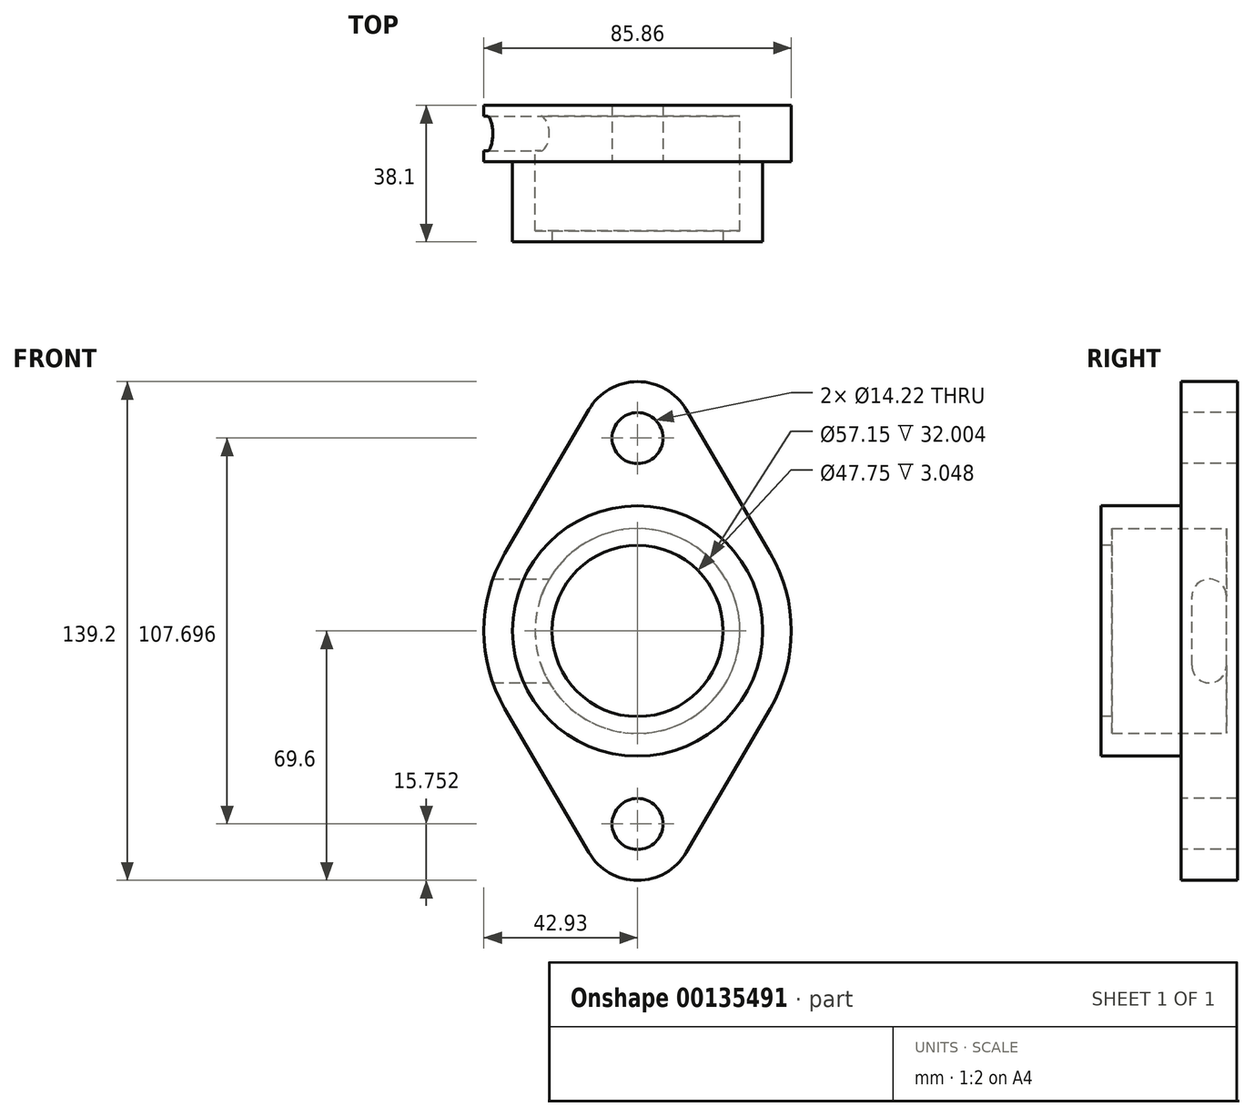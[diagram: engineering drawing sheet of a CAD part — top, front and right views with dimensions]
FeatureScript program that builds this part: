
annotation { "Feature Type Name" : "Feature", "Feature Type Description" : "" }
export const myFeature = defineFeature(function(context is Context, id is Id, definition is map)
    precondition{}
    {
        {
            var Q0;
            Q0=qCreatedBy(makeId("Front.planeOp"),FACE);
            var sketch = newSketch(context, id + "F0", { "sketchPlane" : qUnion([Q0])});
            skCircle(sketch, "E0", {"center": v(0, 0) * mm, "radius": 34.93 * mm});
            skCircle(sketch, "E1", {"center": v(0, 53.85) * mm, "radius": 7.11 * mm});
            skCircle(sketch, "E2", {"center": v(0, -53.85) * mm, "radius": 7.11 * mm});
            skLineSegment(sketch, "E3", {"start": v(-37.06, 21.67) * mm, "end": v(-13.6, 61.8) * mm});
            skLineSegment(sketch, "E4", {"start": v(37.06, 21.67) * mm, "end": v(13.6, 61.8) * mm});
            skLineSegment(sketch, "E5", {"start": v(-37.06, -21.67) * mm, "end": v(-13.6, -61.8) * mm});
            skLineSegment(sketch, "E6", {"start": v(37.06, -21.67) * mm, "end": v(13.6, -61.8) * mm});
            skArc(sketch, "E7", {"start": v(-37.06, 21.67) * mm, "mid": v(-42.93, 0) * mm, "end": v(-37.06, -21.67) * mm});
            skArc(sketch, "E8", {"start": v(-13.6, -61.8) * mm, "mid": v(0, -69.6) * mm, "end": v(13.6, -61.8) * mm});
            skArc(sketch, "E9", {"start": v(37.06, -21.67) * mm, "mid": v(42.93, 0) * mm, "end": v(37.06, 21.67) * mm});
            skArc(sketch, "E10", {"start": v(-13.6, 61.8) * mm, "mid": v(0, 69.6) * mm, "end": v(13.6, 61.8) * mm});
            skSolve(sketch);
        }
        {
            var Q0;
            Q0=makeQuery(id+"F0.imprint","IMPRINT",FACE,{"disambiguationData":[TD([[makeQuery(id+"F0.imprint","IMPRINT",EDGE,{"derivedFrom":sQuery(id+"F0.wireOp",EDGE,"E0")}),1.0]])]});
            extrude(context, id + "F1", {"entities" : qUnion([Q0]), "endBound" : BoundingType.SYMMETRIC, "depth" : 31.5 * mm});
        }
        {
            var Q0;
            Q0=makeQuery(id+"F0.imprint","IMPRINT",FACE,{"disambiguationData":[TD([[makeQuery(id+"F0.imprint","IMPRINT",EDGE,{"derivedFrom":sQuery(id+"F0.wireOp",EDGE,"E0")}),-1.0]])]});
            extrude(context, id + "F2", {"entities" : qUnion([Q0]), "operationType" : NewBodyOperationType.ADD, "oppositeDirection" : true, "depth" : 15.75 * mm});
        }
        {
            var Q0;
            Q0=makeQuery(id+"F0.imprint","IMPRINT",FACE,{"disambiguationData":[TD([[makeQuery(id+"F0.imprint","IMPRINT",EDGE,{"derivedFrom":sQuery(id+"F0.wireOp",EDGE,"E0")}),1.0]])]});
            extrude(context, id + "F3", {"entities" : qUnion([Q0]), "operationType" : NewBodyOperationType.ADD, "depth" : 22.35 * mm});
        }
        {
            var Q0;
            Q0=qCreatedBy(makeId("Front.planeOp"),FACE);
            var sketch = newSketch(context, id + "F4", { "sketchPlane" : qUnion([Q0])});
            skCircle(sketch, "E11", {"center": v(0, 0) * mm, "radius": 28.58 * mm});
            skSolve(sketch);
        }
        {
            var Q0;
            Q0 = qSketchRegion(id + "F4", true);
            extrude(context, id + "F5", {"entities" : qUnion([Q0]), "operationType" : NewBodyOperationType.REMOVE, "depth" : 19.3 * mm});
        }
        {
            var Q0;
            Q0=makeQuery(id+"F3.opExtrude","CAP_FACE",FACE,{"disambiguationData":[OSD([sQuery(id+"F0.wireOp",EDGE,"E0")])],"isStart":false});
            cPlane(context, id + "F6", {"entities" : qUnion([Q0]), "cplaneType" : CPlaneType.OFFSET, "offset" : 0 * mm, "width" : 152.4 * mm, "height" : 152.4 * mm});
        }
        {
            var Q0;
            Q0=qCreatedBy(id+"F6.planeOp",FACE);
            var sketch = newSketch(context, id + "F7", { "sketchPlane" : qUnion([Q0])});
            skCircle(sketch, "E12", {"center": v(0, 0) * mm, "radius": 23.88 * mm});
            skSolve(sketch);
        }
        {
            var Q0;
            Q0 = qSketchRegion(id + "F7", true);
            extrude(context, id + "F8", {"entities" : qUnion([Q0]), "operationType" : NewBodyOperationType.REMOVE, "oppositeDirection" : true, "depth" : 3.05 * mm});
        }
        {
            var Q0;
            Q0=qCreatedBy(makeId("Right.planeOp"),FACE);
            var sketch = newSketch(context, id + "F9", { "sketchPlane" : qUnion([Q0])});
            skLineSegment(sketch, "E13", {"start": v(12.7, -9.65) * mm, "end": v(12.7, 9.65) * mm});
            skLineSegment(sketch, "E14", {"start": v(3.05, -9.65) * mm, "end": v(3.05, 9.65) * mm});
            skArc(sketch, "E15", {"start": v(12.7, 9.65) * mm, "mid": v(7.87, 14.48) * mm, "end": v(3.05, 9.65) * mm});
            skArc(sketch, "E16", {"start": v(12.7, -9.65) * mm, "mid": v(7.87, -14.48) * mm, "end": v(3.05, -9.65) * mm});
            skSolve(sketch);
        }
        {
            var Q0;
            Q0 = qSketchRegion(id + "F9", true);
            extrude(context, id + "F10", {"entities" : qUnion([Q0]), "operationType" : NewBodyOperationType.REMOVE, "endBound" : BoundingType.UP_TO_NEXT, "oppositeDirection" : true, "depth" : 25.4 * mm});
        }
        {
            var Q0;
            Q0=makeQuery(id+"F4.imprint","IMPRINT",FACE,{"disambiguationData":[TD([[makeQuery(id+"F4.imprint","IMPRINT",EDGE,{"derivedFrom":sQuery(id+"F4.wireOp",EDGE,"E11")}),1.0]])]});
            extrude(context, id + "F11", {"entities" : qUnion([Q0]), "operationType" : NewBodyOperationType.REMOVE, "oppositeDirection" : true, "depth" : 12.7 * mm});
        }
    });
